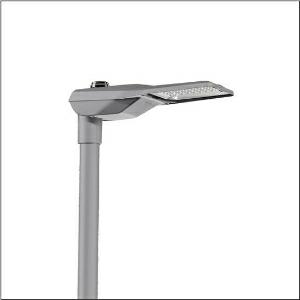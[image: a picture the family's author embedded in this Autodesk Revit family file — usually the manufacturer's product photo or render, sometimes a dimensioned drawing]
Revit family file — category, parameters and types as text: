
# Revit family: streetlight_sl_21_mini___st0_5a_5xe6b37n08gb_187f
name_source: partatom
category: Lighting Fixtures
units: mm (PartAtom-declared; Revit-internal decimal feet)

## family parameters
Cut with Voids When Loaded = No
Host = Face
Light Source = No
Part Type = Normal
Room Calculation Point = No
Round Connector Dimension = Use Diameter
Shared = No

## types (1)
- --- (1 x LED, 5940 lm, 40.4 W, 3000K)
    Apparent Load = 40 VA
    CIE Flux Codes = 41 75 97 100 100
    Color Rendering = 70
    Color Temperature = 3000K
    Default Elevation = 1800 mm
    Description = Streetlight SL 21 mini, mast luminaire, primary light control with lens, of PMMA, primary optical cover: cover, of toughened safety glass, transparent, light distribution: ST0.5a, light emission: direct distribution, primary light characteristic: asymmetric, installation type: side-entry, LED, 3G 1.5mm², High Power LED, rated luminous flux: 5.940lm, luminous efficacy: 147lm/W, light colour: 730, colour temperature: 3000K, control gear: NEMA (7pin), control: overheat protection, pre-setting: linear dimming characteristic, constant luminous flux control, time-dependent luminous flux control, flexible luminous flux parameterisation, mains connection: 230..240V, AC, 50/60Hz, connection cable pre-assembled, cable length: 8,5m, wiring characteristics: H07RN-F, start of lifetime: 40W, end of service life: 41W, reduction: 19W, luminaire housing, of diecast aluminium (EN AC-44300), powder-coated, SITECO metallic grey (DB 702S), corrosivity category C5 high according to DIN EN ISO 12944, multi-level sealing system, sealing non-destructively replaceable, inclination adjustable: 0°, 5°, 10°, 15°, length: 628mm, width: 235mm, height: 110mm, spigot size: 42mm (side-entry), mounting height: 4..8m, protection rating (complete): IP66, insulation class (complete): insulation class I (protective earthing), certification: CE, ENEC, ENEC+, VDE, impact resistance: IK10, permissible operating ambient temperature for outdoor applications: -40..+50°C, standard-compliant lighting for roads and squares, packaging unit: 1 piece

Light Distribution: ST0.5a
    Height = 110 mm
    Lamp = 1 x LED
    Lamp Light Flux = 5940 lm
    Lamp Power = 40.4 W
    Lamp count = 1
    Length = 625 mm
    Luminous efficacy = 147 lm/W
    Manufacturer = Siteco
    ModVariant = No
    Model = 5XE6B37N08GB
    Number of Poles = 1
    OnlyDefault = Yes
    Power Factor = 1
    Product Name = Streetlight SL 21 mini | ST0.5a
    Product group = mast luminaire | pylon top
    ProductGroupID = 6100
    Protection Class = Protection class I
    Protection Degree = IP 66
    RLX_Detail_Level = 1
    RLX_Emergency_Light_Flux = 0 lm
    RLX_Emergency_Type = 0
    RLX_Emergency_Type_DB = No
    RlxData = <blob elided: 36837 chars, md5=222c2c24>
    Socket = socket
    Standby Power = 0 W
    System Light Flux = 5940 lm
    System Power = 40 W
    Type Comments = factory setting: luminous flux: 100 % | dim-lin: 254 | 812 mA
    Type Image = l_1294379.jpg
    URL = http://relux.com
    VarID = @adj_137031
    Voltage = 0 V
    Weight = 0.00 kg
    Width = 234 mm

## geometry (parser evidence)
native form markers: Blend x4, Sweep x8
no freeform markers — native parametric forms only
